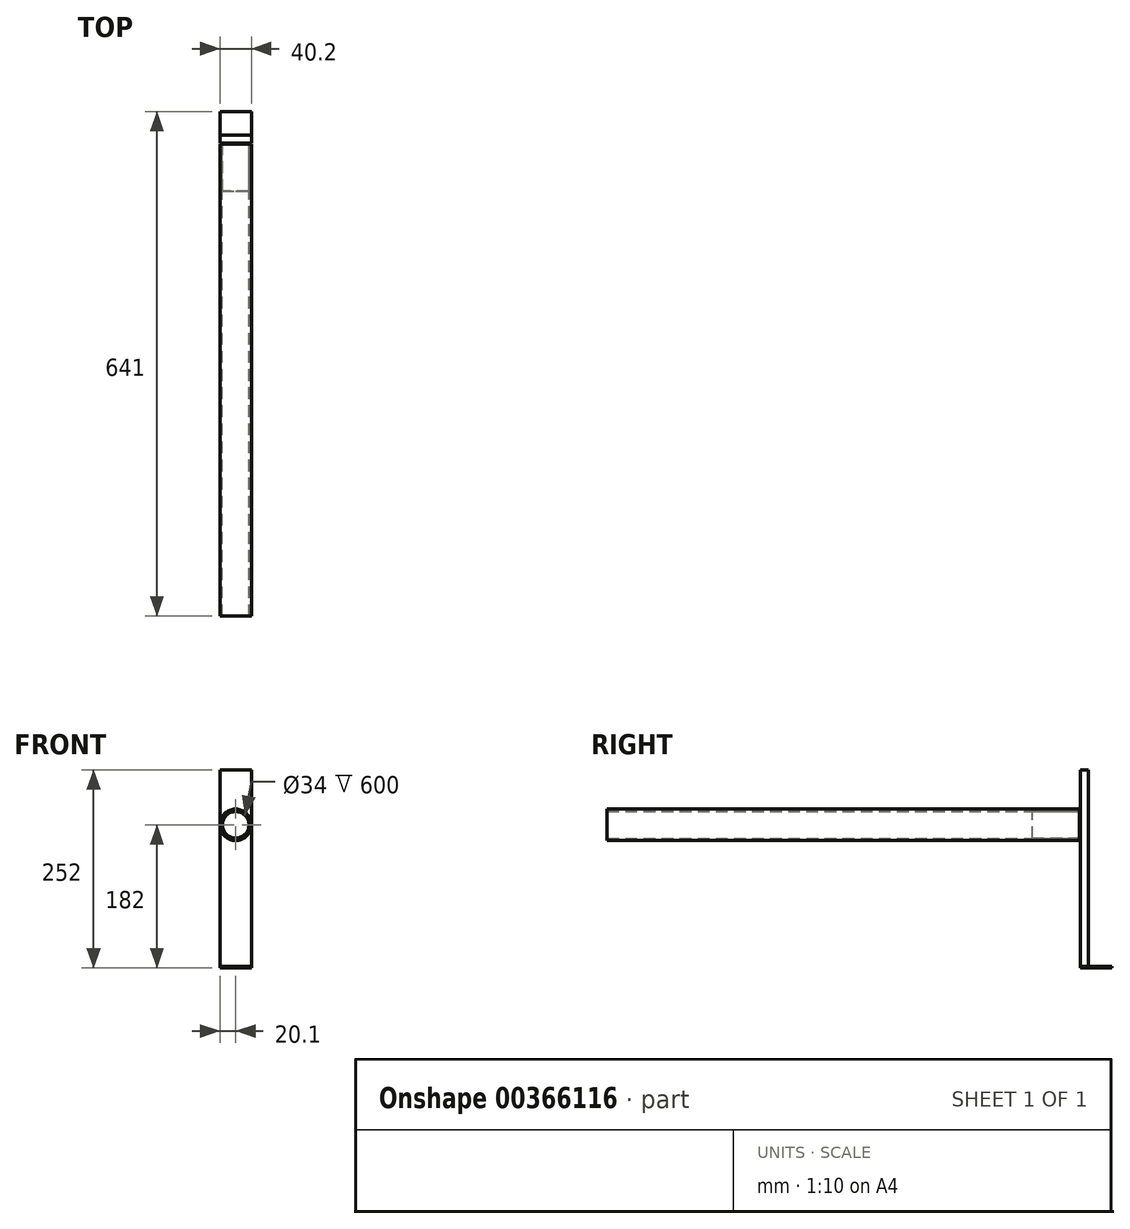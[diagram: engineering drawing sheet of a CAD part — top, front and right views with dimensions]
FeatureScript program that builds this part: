
annotation { "Feature Type Name" : "Feature", "Feature Type Description" : "" }
export const myFeature = defineFeature(function(context is Context, id is Id, definition is map)
    precondition{}
    {
        {
            var Q0;
            Q0=qCreatedBy(makeId("Front.planeOp"),FACE);
            var sketch = newSketch(context, id + "F0", { "sketchPlane" : qUnion([Q0])});
            skCircle(sketch, "E0", {"center": v(0, 0) * mm, "radius": 20 * mm});
            skCircle(sketch, "E1", {"center": v(0, 0) * mm, "radius": 17 * mm});
            skSolve(sketch);
        }
        {
            var Q0;
            Q0=qCreatedBy(makeId("Front.planeOp"),FACE);
            var sketch = newSketch(context, id + "F1", { "sketchPlane" : qUnion([Q0])});
            skCircle(sketch, "E2", {"center": v(0, 0) * mm, "radius": 16.9 * mm});
            skSolve(sketch);
        }
        {
            var Q0;
            Q0=makeQuery(id+"F1.imprint","IMPRINT",FACE,{"disambiguationData":[TD([[makeQuery(id+"F1.imprint","IMPRINT",EDGE,{"derivedFrom":sQuery(id+"F1.wireOp",EDGE,"E2")}),1.0]])]});
            extrude(context, id + "F2", {"entities" : qUnion([Q0]), "depth" : 60 * mm});
        }
        {
            var Q0;
            Q0=makeQuery(id+"F2.opExtrude","CAP_FACE",FACE,{"disambiguationData":[OSD([sQuery(id+"F1.wireOp",EDGE,"E2")])],"isStart":true});
            extrude(context, id + "F3", {"entities" : qUnion([Q0]), "operationType" : NewBodyOperationType.ADD, "depth" : 1 * mm});
        }
        {
            var Q0;
            Q0=makeQuery(id+"F3.opExtrude","CAP_FACE",FACE,{"disambiguationData":[OSD([sQuery(id+"F1.wireOp",EDGE,"E2")])],"isStart":false});
            var sketch = newSketch(context, id + "F4", { "sketchPlane" : qUnion([Q0])});
            skLineSegment(sketch, "E3.top", {"start": v(-20, -180) * mm, "end": v(20, -180) * mm});
            skLineSegment(sketch, "E3.left", {"start": v(-20, 20) * mm, "end": v(-20, -180) * mm});
            skLineSegment(sketch, "E3.right", {"start": v(20, 20) * mm, "end": v(20, -180) * mm});
            skLineSegment(sketch, "E4", {"start": v(-20, 20) * mm, "end": v(-20, 70) * mm});
            skLineSegment(sketch, "E5", {"start": v(-20, 70) * mm, "end": v(20, 70) * mm});
            skLineSegment(sketch, "E6", {"start": v(20, 70) * mm, "end": v(20, 20) * mm});
            skSolve(sketch);
        }
        {
            var Q0;
            Q0 = qSketchRegion(id + "F4", true);
            extrude(context, id + "F5", {"entities" : qUnion([Q0]), "operationType" : NewBodyOperationType.ADD, "depth" : 10 * mm});
        }
        {
            var Q0;
            Q0=makeQuery(id+"F0.imprint","IMPRINT",FACE,{"disambiguationData":[TD([[makeQuery(id+"F0.imprint","IMPRINT",EDGE,{"derivedFrom":sQuery(id+"F0.wireOp",EDGE,"E0")}),1.0]])]});
            extrude(context, id + "F6", {"entities" : qUnion([Q0]), "operationType" : NewBodyOperationType.ADD, "depth" : 600 * mm});
        }
        {
            var Q0;
            Q0=makeQuery(id+"F5.opExtrude","SWEPT_FACE",FACE,{"disambiguationData":[OSD([sQuery(id+"F4.wireOp",EDGE,"E3.top")])]});
            var sketch = newSketch(context, id + "F7", { "sketchPlane" : qUnion([Q0])});
            skLineSegment(sketch, "E7.top", {"start": v(-20, -41) * mm, "end": v(20, -41) * mm});
            skLineSegment(sketch, "E8", {"start": v(-20.1, -0.9) * mm, "end": v(20.1, -0.9) * mm});
            skLineSegment(sketch, "E9", {"start": v(20.1, -0.9) * mm, "end": v(20, -41) * mm});
            skLineSegment(sketch, "E10", {"start": v(-20.1, -0.9) * mm, "end": v(-20, -41) * mm});
            skSolve(sketch);
        }
        {
            var Q0;
            Q0 = qSketchRegion(id + "F7", true);
            extrude(context, id + "F8", {"entities" : qUnion([Q0]), "operationType" : NewBodyOperationType.ADD, "depth" : 2 * mm});
        }
    });
